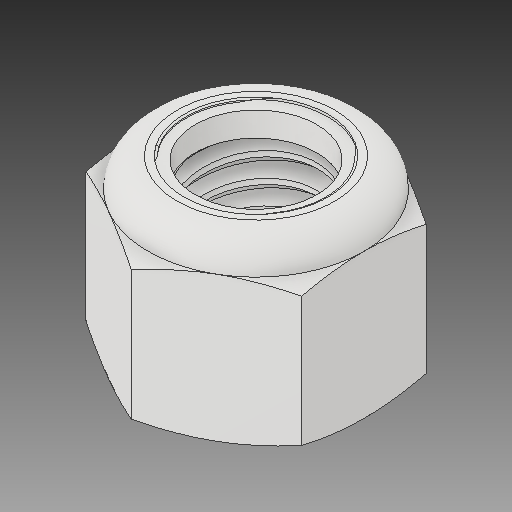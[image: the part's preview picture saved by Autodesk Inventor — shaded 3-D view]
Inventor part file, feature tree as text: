
AUTODESK INVENTOR PART (.ipt)
format: ipt  version: 2018.2 (Build 222227000, 227)  size: 336,896 bytes
history: native  units: in
note: dims shown in document units (in); Inventor stores cm internally (conversion verified against a paired STEP export)
features: other x1, revolve x1
ambient origin geometry x8: Origin, YZ Plane, XZ Plane, XY Plane, X Axis, Y Axis, Z Axis, Center Point
bodies: Solid1 (feature_tree), Solid2 (feature_tree)
feature tree (2):
  other  "Cut-Revolve4"
  revolve  "Revolve2"  [1 undecoded]
note: 1 required parameter value undecoded (feature->parameter linkage not recoverable at this tier; creation-order binding heuristic only, values carry confidence <= 0.55)
